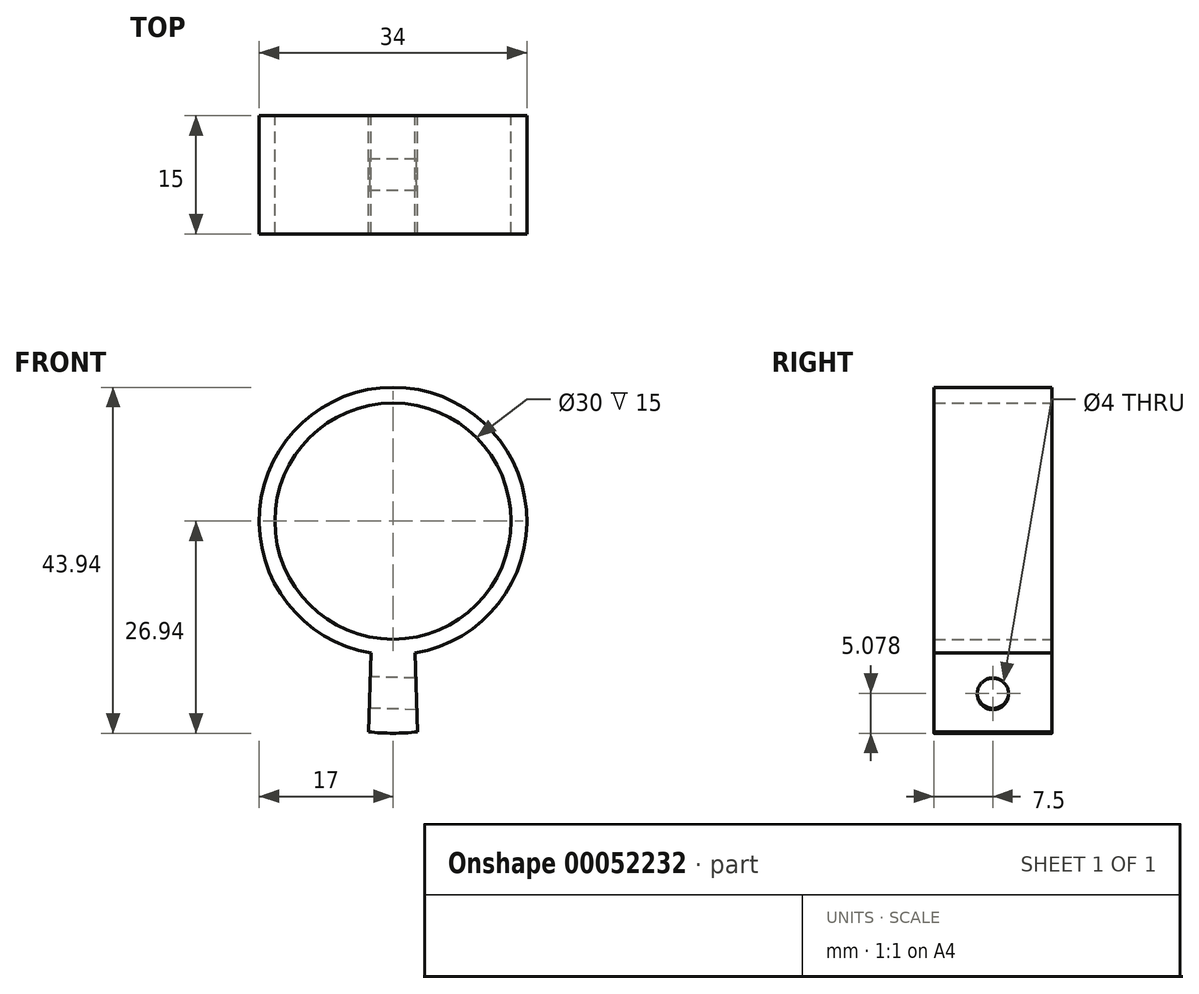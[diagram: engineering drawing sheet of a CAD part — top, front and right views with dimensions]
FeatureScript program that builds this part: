
annotation { "Feature Type Name" : "Feature", "Feature Type Description" : "" }
export const myFeature = defineFeature(function(context is Context, id is Id, definition is map)
    precondition{}
    {
        {
            var Q0;
            Q0=qCreatedBy(makeId("Front.planeOp"),FACE);
            var sketch = newSketch(context, id + "F0", { "sketchPlane" : qUnion([Q0])});
            skCircle(sketch, "E0", {"center": v(0, 0) * mm, "radius": 15 * mm});
            skCircle(sketch, "E1.0", {"center": v(0, 0) * mm, "radius": 17 * mm});
            skSolve(sketch);
        }
        {
            var Q0;
            Q0=makeQuery(id+"F0.imprint","IMPRINT",FACE,{"disambiguationData":[TD([[makeQuery(id+"F0.imprint","IMPRINT",EDGE,{"derivedFrom":sQuery(id+"F0.wireOp",EDGE,"E0")}),-1.0]])]});
            extrude(context, id + "F1", {"entities" : qUnion([Q0]), "depth" : 15 * mm});
        }
        {
            var Q0;
            Q0=makeQuery(id+"F1.opExtrude","CAP_FACE",FACE,{"disambiguationData":[OSD([sQuery(id+"F0.wireOp",EDGE,"E0"),sQuery(id+"F0.wireOp",EDGE,"E1.0")])],"isStart":true});
            var sketch = newSketch(context, id + "F2", { "sketchPlane" : qUnion([Q0])});
            skArc(sketch, "E2", {"start": v(-3.1, -26.76) * mm, "mid": v(-1.55, -26.9) * mm, "end": v(0, -26.94) * mm});
            skArc(sketch, "E3", {"start": v(-2.8, -16.77) * mm, "mid": v(-1.4, -16.94) * mm, "end": v(0, -17) * mm});
            skLineSegment(sketch, "E4", {"start": v(0, -13.28) * mm, "end": v(0, -26.94) * mm, "construction": true});
            skLineSegment(sketch, "E5", {"start": v(-2.8, -16.77) * mm, "end": v(-3.1, -26.76) * mm});
            skArc(sketch, "E6.MirrorCS", {"start": v(2.8, -16.77) * mm, "mid": v(1.4, -16.94) * mm, "end": v(0, -17) * mm});
            skLineSegment(sketch, "E7.MirrorCS", {"start": v(2.8, -16.77) * mm, "end": v(3.1, -26.76) * mm});
            skArc(sketch, "E8.MirrorCS", {"start": v(3.1, -26.76) * mm, "mid": v(1.55, -26.9) * mm, "end": v(0, -26.94) * mm});
            skSolve(sketch);
        }
        {
            var Q0;
            Q0=makeQuery(id+"F2.imprint","IMPRINT",FACE,{"disambiguationData":[TD([[makeQuery(id+"F2.imprint","IMPRINT",EDGE,{"derivedFrom":sQuery(id+"F2.wireOp",EDGE,"E2")}),1.0]])]});
            extrude(context, id + "F3", {"entities" : qUnion([Q0]), "operationType" : NewBodyOperationType.ADD, "oppositeDirection" : true, "depth" : 15 * mm});
        }
        {
            var Q0;
            Q0=makeQuery(id+"F3.opExtrude","SWEPT_FACE",FACE,{"disambiguationData":[OSD([sQuery(id+"F2.wireOp",EDGE,"E7.MirrorCS")])]});
            var sketch = newSketch(context, id + "F4", { "sketchPlane" : qUnion([Q0])});
            skCircle(sketch, "E9", {"center": v(7.5, -21.85) * mm, "radius": 2 * mm});
            skSolve(sketch);
        }
        {
            var Q0;
            Q0=makeQuery(id+"F4.imprint","IMPRINT",FACE,{"disambiguationData":[TD([[makeQuery(id+"F4.imprint","IMPRINT",EDGE,{"derivedFrom":sQuery(id+"F4.wireOp",EDGE,"E9")}),1.0]])]});
            extrude(context, id + "F5", {"entities" : qUnion([Q0]), "operationType" : NewBodyOperationType.REMOVE, "endBound" : BoundingType.THROUGH_ALL, "oppositeDirection" : true, "depth" : 25 * mm});
        }
    });
